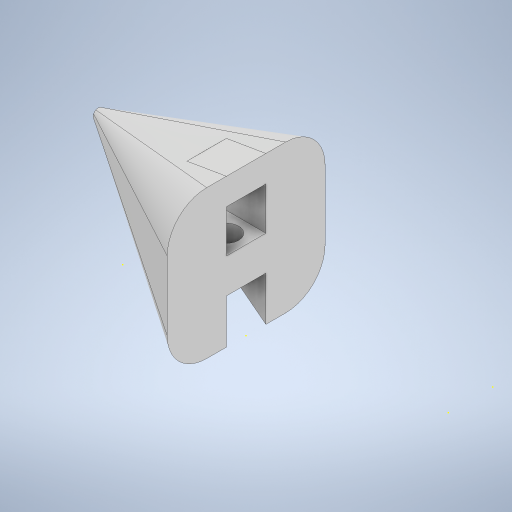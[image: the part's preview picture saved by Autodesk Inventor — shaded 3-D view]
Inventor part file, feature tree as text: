
AUTODESK INVENTOR PART (.ipt)
format: ipt  version: 2024 (Build 280153000, 153)  size: 672,768 bytes
history: native  units: mm
features: sketch x35, extrude x28, plane x4, chamfer x3, split x3, move_body x3, delete_face x1, fillet x1, boolean_combine x1, loft x1, other x1
ambient origin geometry x8: Origin, YZ Plane, XZ Plane, XY Plane, X Axis, Y Axis, Z Axis, Center Point
bodies: Solid1 (feature_tree), Solid2 (feature_tree), Solid3 (feature_tree), Solid4 (feature_tree), Solid5 (feature_tree), Solid6 (feature_tree), Solid7 (feature_tree)
feature tree (81):
  extrude  "Extrusion1"  Depth=16.0mm
  sketch  "Sketch2"  dims[d2=15.0mm d3=0.0mm d4=10.0mm]
  extrude  "Extrusion2"  Depth=10.0mm
  chamfer  "Chamfer1"  Distance=21.25mm
  extrude  "Extrusion3"  Depth=10.0mm TaperAngle=0.0deg
  extrude  "Extrusion4"  Depth=7.0mm TaperAngle=0.0deg
  extrude  "Extrusion5"  Depth=6.0mm TaperAngle=0.0deg
  chamfer  "Chamfer2"  Distance=6.0mm Angle=45.0deg
  sketch  "Sketch6"  dims[d14=7.0mm d15=11.5mm d16=0.0mm]
  extrude  "Extrusion6"  Depth=15.0mm
  extrude  "Extrusion7"  Depth=45.25mm TaperAngle=0.0deg
  chamfer  "Chamfer3"  Distance=11.5mm Angle=45.0deg
  sketch  "Sketch9"  dims[d26=3.3mm d27=45.25mm d28=0.0mm d29=11.5mm d30=5.5mm d31=45.0deg]
  extrude  "Extrusion8"  Depth=65.75mm TaperAngle=0.0deg
  extrude  "Extrusion9"  Depth=9.0mm TaperAngle=0.0deg
  extrude  "Extrusion10"  Depth=13.0mm TaperAngle=0.0deg
  sketch  "Sketch13"  dims[d43=24.0mm d44=21.0mm d45=0.0mm]
  extrude  "Extrusion11"  Depth=21.0mm TaperAngle=0.0deg
  extrude  "Extrusion12"  TaperAngle=0.0deg  [1 undecoded]
  extrude  "Extrusion13"  Depth=4.0mm
  plane  "Work Plane1"
  split  "Split1"
  move_body  "Move Body1"
  extrude  "Extrusion14"  Depth=1.0mm
  delete_face  "Delete Face1"
  fillet  "Fillet1"  Radius=1.5mm
  extrude  "Extrusion17"  Depth=1.0mm
  extrude  "Extrusion18"  Depth=1.2mm TaperAngle=0.0deg
  extrude  "Extrusion19"  [1 undecoded]
  extrude  "Extrusion20"  Depth=3.0mm TaperAngle=0.0deg
  plane  "Work Plane2"
  split  "Split2"
  move_body  "Move Body2"
  extrude  "Extrusion21"  Depth=15.0mm
  boolean_combine  "Combine1"
  plane  "Work Plane3"
  sketch  "Sketch26"  dims[d85=-15.0mm d86=-10.0mm d87=0.0mm d88=0.0mm]
  loft  "Loft1"
  plane  "Work Plane4"
  split  "Split3"
  move_body  "Move Body3"
  extrude  "Extrusion22"  TaperAngle=0.0deg  [1 undecoded]
  extrude  "Extrusion23"  Depth=4.0mm
  extrude  "Extrusion24"  Depth=4.0mm
  sketch  "Sketch31"  dims[d100=4.0mm d101=0.0mm d102=0.75mm d103=0.0mm]
  sketch  "Sketch32"  dims[d104=4.0mm d105=0.0mm d106=1.0mm]
  extrude  "Extrusion25"  Depth=4.0mm
  extrude  "Extrusion26"  Depth=2.0mm
  extrude  "Extrusion27"  Depth=4.0mm TaperAngle=0.0deg
  extrude  "Extrusion28"  Depth=4.0mm
  extrude  "Extrusion29"  Depth=4.0mm TaperAngle=0.0deg
  extrude  "Extrusion30"  Depth=4.0mm TaperAngle=0.0deg
  sketch  "Sketch39"
  sketch  "Sketch1"  dims[d0=36.0mm d1=16.0mm]
  sketch  "Sketch3"  dims[d5=10.0mm]
  sketch  "Sketch4"  dims[d6=3.3mm d7=21.25mm d8=0.0mm]
  sketch  "Sketch5"  dims[d9=10.0mm d10=5.5mm d11=45.0deg d12=10.0mm d13=0.0mm]
  sketch  "Sketch7"  dims[d17=3.3mm d18=1.0mm d19=0.0mm d20=6.0mm d21=11.5mm d22=45.0deg]
  sketch  "Sketch8"  dims[d23=15.0mm d24=0.0mm d25=9.0mm]
  sketch  "Sketch10"  dims[d32=2.0mm d33=65.75mm d34=0.0mm]
  sketch  "Sketch11"  dims[d35=0.5mm d36=0.0mm d37=9.0mm d38=0.0mm]
  sketch  "Sketch12"  dims[d39=0.5mm d40=0.0mm d41=13.0mm d42=0.0mm]
  sketch  "Sketch14"  dims[d46=12.25mm d47=-12.0mm d48=0.0mm d49=0.0mm]
  sketch  "Sketch15"  dims[d50=10.0mm d51=0.0mm d52=4.0mm]
  sketch  "Sketch16"  dims[d61=1.0mm d62=1.0mm d63=1.5mm d64=0.0mm]
  sketch  "Sketch17"  dims[d65=1.0mm d66=1.0mm]
  sketch  "Sketch20"  dims[d67=5.5mm d68=0.0mm d69=1.2mm d70=0.0mm]
  sketch  "Sketch21"  dims[d71=2.2mm d72=0.0mm d73=-5.5mm]
  sketch  "Sketch22"  dims[d74=-3.0mm d75=0.0mm d76=0.0mm d77=3.0mm d78=0.0mm]
  sketch  "Sketch23"  dims[d79=15.0mm d80=1.0mm]
  sketch  "Sketch24"  dims[d81=0.0mm d82=90.0deg d83=0.0mm d84=90.0deg]
  sketch  "Sketch27"  dims[d89=4.0mm d90=11.0mm]
  other  "Edges1"
  sketch  "Sketch28"  dims[d91=4.0mm d92=0.0mm d93=4.0mm]
  sketch  "Sketch29"  dims[d94=4.0mm d95=0.0mm d96=2.5mm]
  sketch  "Sketch30"  dims[d97=12.0mm d98=0.0mm d99=2.0mm]
  sketch  "Sketch33"  dims[d107=4.0mm d108=0.0mm d109=5.75mm d110=0.0mm]
  sketch  "Sketch34"  dims[d111=1.5mm d112=4.0mm d113=0.0mm]
  sketch  "Sketch35"  dims[d53=0.872665mm]
  sketch  "Sketch36"
  sketch  "Sketch37"
note: 3 required parameter values undecoded (feature->parameter linkage not recoverable at this tier; creation-order binding heuristic only, values carry confidence <= 0.55)
